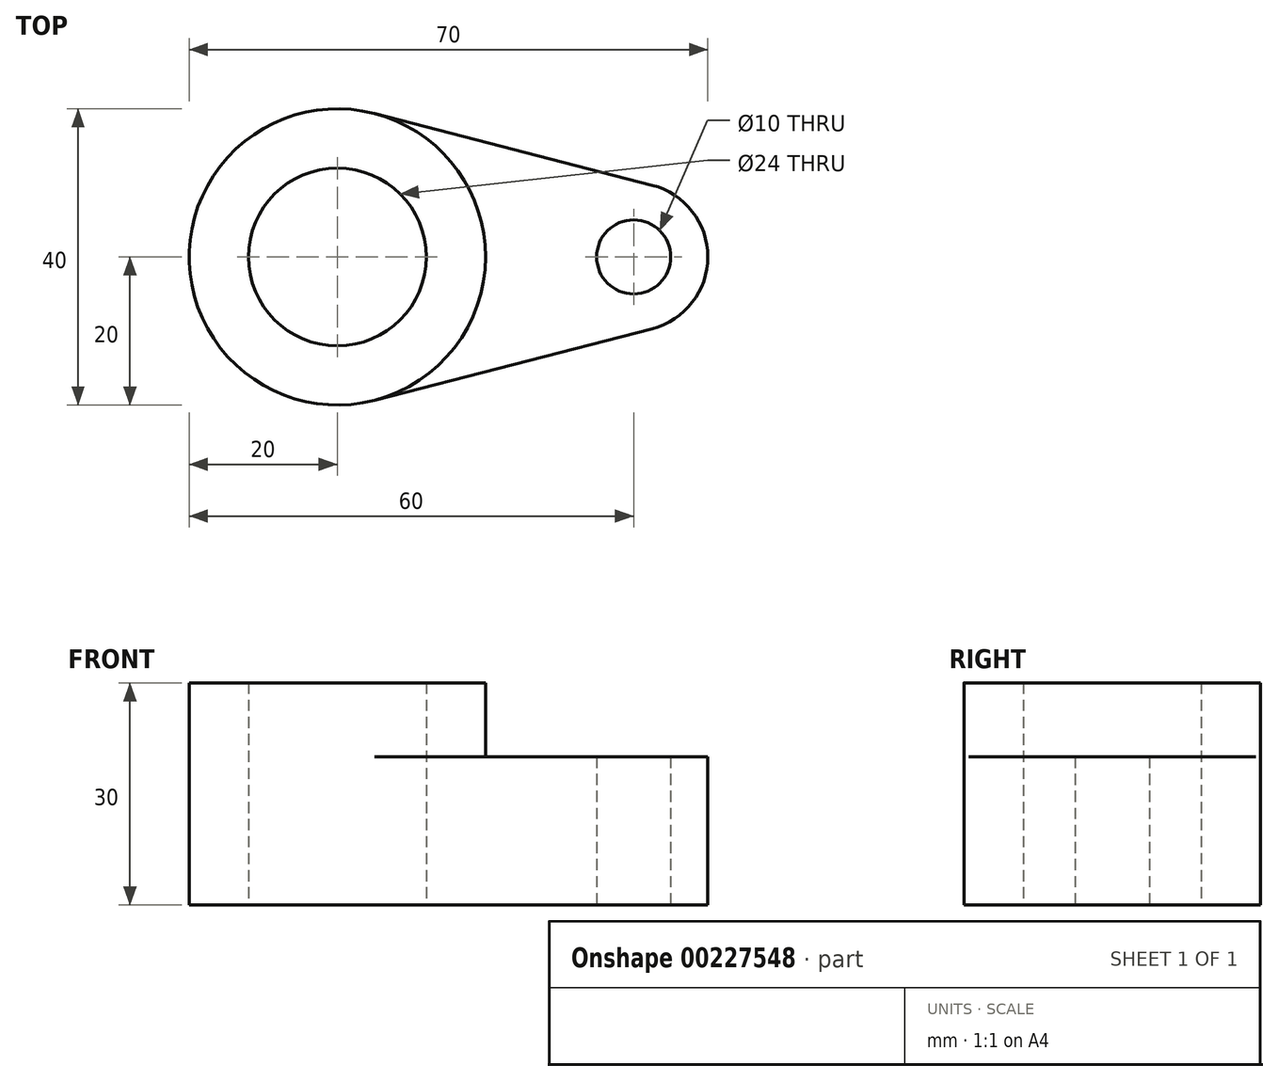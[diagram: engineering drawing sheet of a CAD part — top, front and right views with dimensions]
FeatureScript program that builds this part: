
annotation { "Feature Type Name" : "Feature", "Feature Type Description" : "" }
export const myFeature = defineFeature(function(context is Context, id is Id, definition is map)
    precondition{}
    {
        {
            var Q0;
            Q0=qCreatedBy(makeId("Top.planeOp"),FACE);
            var sketch = newSketch(context, id + "F0", { "sketchPlane" : qUnion([Q0])});
            skCircle(sketch, "E0", {"center": v(0, 0) * mm, "radius": 20 * mm});
            skArc(sketch, "E1", {"start": v(42.5, -9.68) * mm, "mid": v(50, 0) * mm, "end": v(42.5, 9.68) * mm});
            skPoint(sketch, "E2.start.orphan", {"position": v(0, 20) * mm});
            skPoint(sketch, "E3.start.orphan", {"position": v(0, -20) * mm});
            skLineSegment(sketch, "E4", {"start": v(5, 19.36) * mm, "end": v(42.5, 9.68) * mm});
            skLineSegment(sketch, "E5", {"start": v(5, -19.36) * mm, "end": v(42.5, -9.68) * mm});
            skCircle(sketch, "E6", {"center": v(0, 0) * mm, "radius": 12 * mm});
            skCircle(sketch, "E7", {"center": v(40, 0) * mm, "radius": 5 * mm});
            skSolve(sketch);
        }
        {
            var Q0;
            Q0=makeQuery(id+"F0.imprint","IMPRINT",FACE,{"disambiguationData":[TD([[makeQuery(id+"F0.imprint","IMPRINT",EDGE,{"derivedFrom":sQuery(id+"F0.wireOp",EDGE,"E1")}),1.0]])]});
            extrude(context, id + "F1", {"entities" : qUnion([Q0]), "depth" : 15 * mm});
        }
        {
            var Q0;
            Q0=makeQuery(id+"F0.imprint","IMPRINT",FACE,{"disambiguationData":[TD([[makeQuery(id+"F0.imprint","IMPRINT",EDGE,{"derivedFrom":sQuery(id+"F0.wireOp",EDGE,"E6")}),-1.0]])]});
            extrude(context, id + "F2", {"entities" : qUnion([Q0]), "operationType" : NewBodyOperationType.ADD, "depth" : 30 * mm});
        }
        {
            var Q0;
            Q0=makeQuery(id+"F0.imprint","IMPRINT",FACE,{"disambiguationData":[TD([[makeQuery(id+"F0.imprint","IMPRINT",EDGE,{"derivedFrom":sQuery(id+"F0.wireOp",EDGE,"E1")}),1.0]])]});
            extrude(context, id + "F3", {"entities" : qUnion([Q0]), "operationType" : NewBodyOperationType.ADD, "depth" : 20 * mm});
        }
    });
